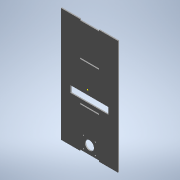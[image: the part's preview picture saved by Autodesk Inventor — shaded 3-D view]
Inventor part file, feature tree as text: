
AUTODESK INVENTOR PART (.ipt)
format: ipt  version: 2020 (Build 240168000, 168)  size: 167,424 bytes
history: native  units: mm (DEFAULTED — no unit token found)
features: sketch x16, extrude x13
ambient origin geometry x8: Origin, YZ Plane, XZ Plane, XY Plane, X Axis, Y Axis, Z Axis, Center Point
bodies: Solid1 (feature_tree)
feature tree (29):
  extrude  "Extrusion1"  Depth=3.0mm
  sketch  "3D Sketch1"
  extrude  "Extrusion2"  Depth=3.0mm TaperAngle=0.0deg
  extrude  "Extrusion3"  Depth=3.0mm TaperAngle=0.0deg
  extrude  "Extrusion4"  Depth=3.0mm TaperAngle=0.0deg
  extrude  "Extrusion5"  Depth=3.0mm TaperAngle=0.0deg
  extrude  "Extrusion6"  Depth=3.0mm TaperAngle=0.0deg
  extrude  "Extrusion7"  Depth=21.5mm TaperAngle=0.0deg
  extrude  "Extrusion8"  [1 undecoded]
  sketch  "Sketch9"
  sketch  "Sketch10"
  extrude  "Extrusion9"  [1 undecoded]
  extrude  "Extrusion10"  [1 undecoded]
  extrude  "Extrusion11"  [1 undecoded]
  extrude  "Extrusion12"  [1 undecoded]
  extrude  "Extrusion13"  [1 undecoded]
  sketch  "Sketch1"  dims[d2=3.0mm d3=0.0mm d9=50.0mm]
  sketch  "Sketch2"  dims[d14=3.0mm d15=0.0mm d21=3.0mm d22=0.0mm]
  sketch  "Sketch3"  dims[d25=3.0mm d26=0.0mm d31=3.0mm d32=0.0mm]
  sketch  "Sketch4"  dims[d37=3.0mm d38=0.0mm d45=3.0mm d46=0.0mm]
  sketch  "Sketch5"  dims[d58=3.0mm d59=0.0mm d67=10.5mm d68=0.0mm]
  sketch  "Sketch6"  dims[d69=11.75mm d70=0.0mm d71=3.0mm d72=0.0mm]
  sketch  "Sketch7"  dims[d73=16.25mm d74=0.0mm d85=21.5mm d86=0.0mm]
  sketch  "Sketch8"
  sketch  "Sketch11"
  sketch  "Sketch12"
  sketch  "Sketch13"
  sketch  "Sketch14"
  sketch  "Sketch15"
note: 6 required parameter values undecoded (feature->parameter linkage not recoverable at this tier; creation-order binding heuristic only, values carry confidence <= 0.55)
